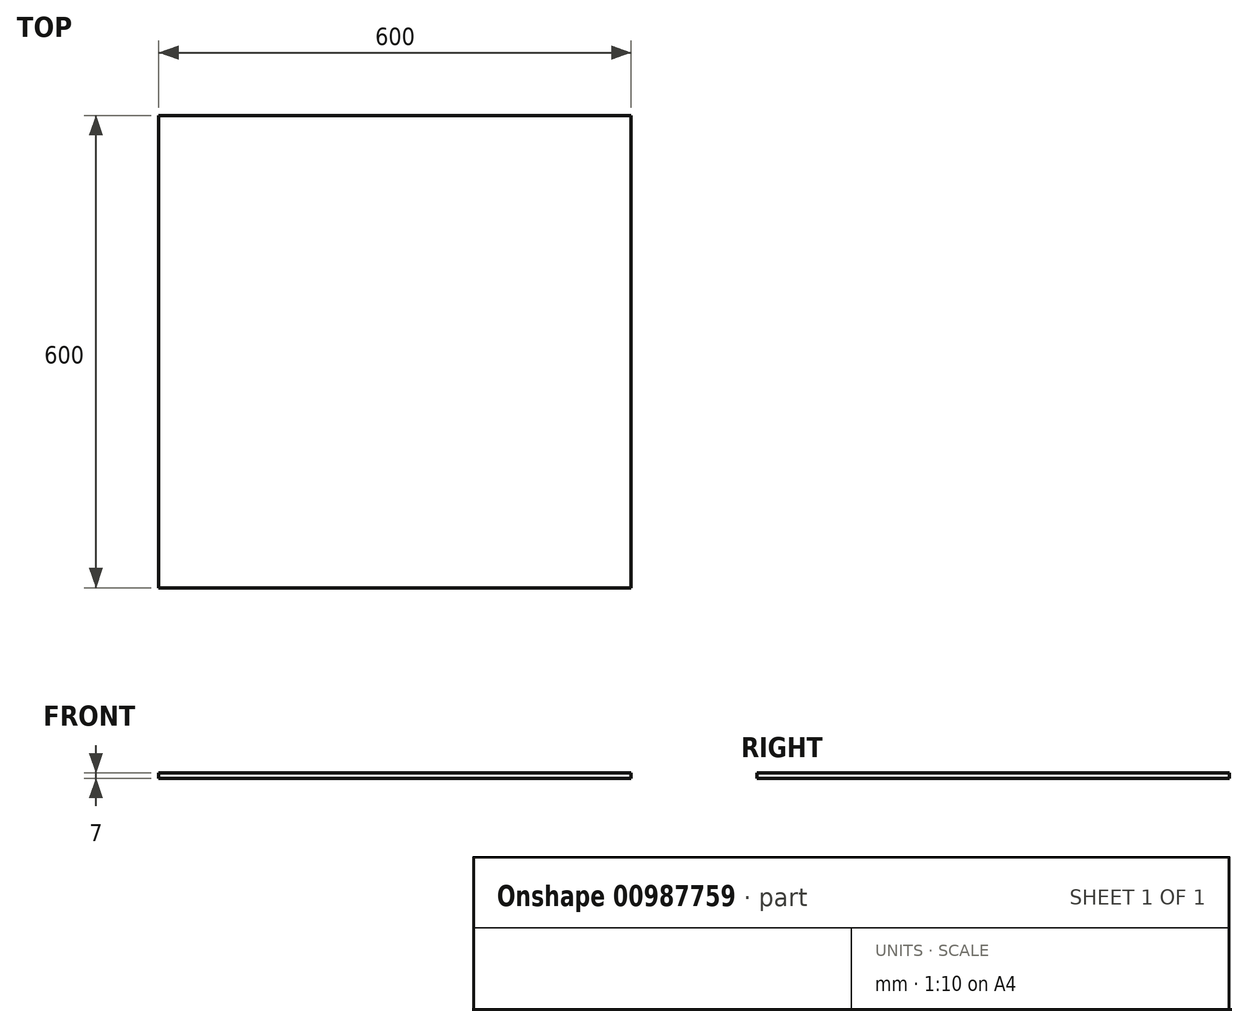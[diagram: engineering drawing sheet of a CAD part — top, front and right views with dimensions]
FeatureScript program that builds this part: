
annotation { "Feature Type Name" : "Feature", "Feature Type Description" : "" }
export const myFeature = defineFeature(function(context is Context, id is Id, definition is map)
    precondition{}
    {
        {
            var Q0;
            Q0=qCreatedBy(makeId("Top.planeOp"),FACE);
            var sketch = newSketch(context, id + "F0", { "sketchPlane" : qUnion([Q0])});
            skLineSegment(sketch, "E0.bottom", {"start": v(300, -300) * mm, "end": v(-300, -300) * mm});
            skLineSegment(sketch, "E0.top", {"start": v(300, 300) * mm, "end": v(-300, 300) * mm});
            skLineSegment(sketch, "E0.left", {"start": v(300, -300) * mm, "end": v(300, 300) * mm});
            skLineSegment(sketch, "E0.right", {"start": v(-300, -300) * mm, "end": v(-300, 300) * mm});
            skPoint(sketch, "E0.middle", {"position": v(0, 0) * mm});
            skSolve(sketch);
        }
        {
            var Q0;
            Q0 = qSketchRegion(id + "F0", true);
            extrude(context, id + "F1", {"entities" : qUnion([Q0]), "depth" : 7 * mm, "offsetDistance" : 25 * mm});
        }
    });
